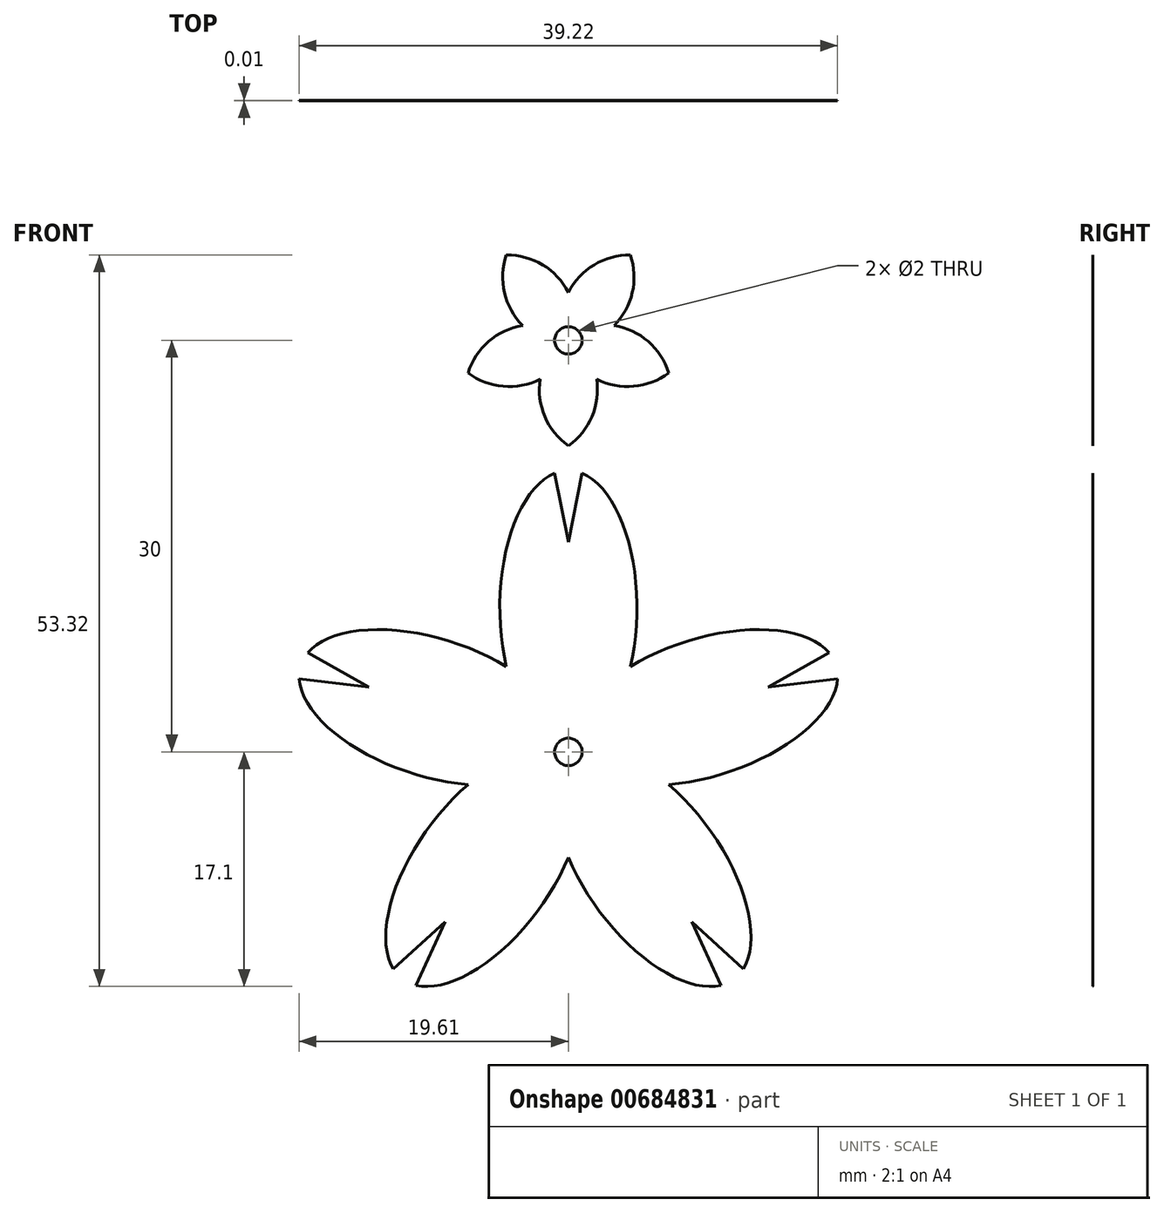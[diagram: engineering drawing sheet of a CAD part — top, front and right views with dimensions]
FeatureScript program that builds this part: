
annotation { "Feature Type Name" : "Feature", "Feature Type Description" : "" }
export const myFeature = defineFeature(function(context is Context, id is Id, definition is map)
    precondition{}
    {
        {
            var Q0;
            Q0=qCreatedBy(makeId("Front.planeOp"),FACE);
            var sketch = newSketch(context, id + "F0", { "sketchPlane" : qUnion([Q0])});
            skEllipticalArc(sketch, "E0", {});
            skLineSegment(sketch, "E1", {"start": v(0, 15.3) * mm, "end": v(1, 20.3) * mm});
            skLineSegment(sketch, "E2.MirrorCS", {"start": v(0, 15.3) * mm, "end": v(-1, 20.3) * mm});
            skEllipticalArc(sketch, "E3.1.0", {});
            skLineSegment(sketch, "E3.1.1", {"start": v(-14.55, 4.73) * mm, "end": v(-19.61, 5.32) * mm});
            skLineSegment(sketch, "E3.1.2", {"start": v(-14.55, 4.73) * mm, "end": v(-19, 7.22) * mm});
            skEllipticalArc(sketch, "E3.2.0", {});
            skLineSegment(sketch, "E3.2.1", {"start": v(-9, -12.38) * mm, "end": v(-11.12, -17) * mm});
            skLineSegment(sketch, "E3.2.2", {"start": v(-9, -12.38) * mm, "end": v(-12.74, -15.83) * mm});
            skEllipticalArc(sketch, "E3.3.0", {});
            skLineSegment(sketch, "E3.3.1", {"start": v(9, -12.38) * mm, "end": v(12.74, -15.83) * mm});
            skLineSegment(sketch, "E3.3.2", {"start": v(9, -12.38) * mm, "end": v(11.12, -17) * mm});
            skEllipticalArc(sketch, "E3.4.0", {});
            skLineSegment(sketch, "E3.4.1", {"start": v(14.55, 4.73) * mm, "end": v(19, 7.22) * mm});
            skLineSegment(sketch, "E3.4.2", {"start": v(14.55, 4.73) * mm, "end": v(19.61, 5.32) * mm});
            skPoint(sketch, "E3.center", {"position": v(0, 0) * mm});
            const initialGuessF0  = {"E0": [0, 0.0105, 0, 1, 0.01, 0.005, 0.20135792079033113, 6.081827386389255], "E3.1.0": [-0.009986093421099114, 0.0032446784409369493, -0.9510565162951536, 0.30901699437494723, 0.01, 0.005, 0.20135792079033066, 6.0818273863892545], "E3.2.0": [-0.006171745149070969, -0.008494678440936947, -0.587785252292473, -0.8090169943749476, 0.01, 0.005, 0.20135792079033082, 6.0818273863892545], "E3.3.0": [0.006171745149070967, -0.00849467844093695, 0.5877852522924732, -0.8090169943749473, 0.01, 0.005, 0.20135792079033088, 6.0818273863892545], "E3.4.0": [0.009986093421099114, 0.0032446784409369493, 0.9510565162951536, 0.3090169943749475, 0.01, 0.005, 0.20135792079033107, 6.081827386389255]};
            skSetInitialGuess(sketch, initialGuessF0);
            skSolve(sketch);
        }
        {
            var Q0;
            Q0=qCreatedBy(makeId("Front.planeOp"),FACE);
            var sketch = newSketch(context, id + "F1", { "sketchPlane" : qUnion([Q0])});
            skLineSegment(sketch, "E4.0", {"start": v(0, 15.3) * mm, "end": v(-1, 20.3) * mm});
            skLineSegment(sketch, "E5.0", {"start": v(0, 15.3) * mm, "end": v(1, 20.3) * mm});
            skEllipticalArc(sketch, "E6.0", {});
            skLineSegment(sketch, "E7.0", {"start": v(14.55, 4.73) * mm, "end": v(19, 7.22) * mm});
            skLineSegment(sketch, "E8.0", {"start": v(14.55, 4.73) * mm, "end": v(19.61, 5.32) * mm});
            skEllipticalArc(sketch, "E9.0", {});
            skLineSegment(sketch, "E10.0", {"start": v(9, -12.38) * mm, "end": v(11.12, -17) * mm});
            skLineSegment(sketch, "E11.0", {"start": v(9, -12.38) * mm, "end": v(12.74, -15.83) * mm});
            skEllipticalArc(sketch, "E12.0", {});
            skLineSegment(sketch, "E13.0", {"start": v(-9, -12.38) * mm, "end": v(-12.74, -15.83) * mm});
            skLineSegment(sketch, "E14.0", {"start": v(-9, -12.38) * mm, "end": v(-11.12, -17) * mm});
            skEllipticalArc(sketch, "E15.0", {});
            skLineSegment(sketch, "E16.0", {"start": v(-14.55, 4.73) * mm, "end": v(-19.61, 5.32) * mm});
            skLineSegment(sketch, "E17.0", {"start": v(-14.55, 4.73) * mm, "end": v(-19, 7.22) * mm});
            skEllipticalArc(sketch, "E18.trimOffspring", {});
            skEllipticalArc(sketch, "E19.trimOffspring", {});
            skEllipticalArc(sketch, "E20.trimOffspring", {});
            skEllipticalArc(sketch, "E21.trimOffspring", {});
            skCircle(sketch, "E22", {"center": v(0, 0) * mm, "radius": 1 * mm});
            skEllipticalArc(sketch, "E23.0", {});
            skEllipticalArc(sketch, "E24.MirrorCS", {});
            const initialGuessF1  = {"E6.0": [0.009986093421099114, 0.0032446784409369493, 0.9510565162951536, 0.3090169943749475, 0.01, 0.005, 0.20135792079033046, 2.0131203889968834], "E9.0": [0.006171745149070967, -0.00849467844093695, 0.5877852522924732, -0.8090169943749473, 0.01, 0.005, 0.20135792079033088, 2.0131203889969314], "E12.0": [-0.006171745149070969, -0.008494678440936947, -0.587785252292473, -0.8090169943749476, 0.01, 0.005, 0.20135792079033066, 2.013120388996931], "E15.0": [-0.009986093421099114, 0.0032446784409369493, -0.9510565162951536, 0.30901699437494723, 0.01, 0.005, 0.20135792079033066, 2.0131203889969314], "E18.trimOffspring": [-0.009986093421099114, 0.0032446784409369493, -0.9510565162951536, 0.30901699437494723, 0.01, 0.005, 4.270064918182703, 6.0818273863892545], "E19.trimOffspring": [-0.006171745149070969, -0.008494678440936947, -0.587785252292473, -0.8090169943749476, 0.01, 0.005, 4.270064918182655, 6.081827386389254], "E20.trimOffspring": [0.006171745149070967, -0.00849467844093695, 0.5877852522924732, -0.8090169943749473, 0.01, 0.005, 4.270064918182655, 6.0818273863892545], "E21.trimOffspring": [0.009986093421099114, 0.0032446784409369493, 0.9510565162951536, 0.3090169943749475, 0.01, 0.005, 4.270064918182655, 6.081827386389255], "E23.0": [0, 0.0105, 0, 1, 0.01, 0.005, 0.2013579207903312, 2.0131203889968976], "E24.MirrorCS": [0, 0.0105, 0, 1, 0.01, 0.005, 4.270064918182689, 6.081827386389255]};
            skSetInitialGuess(sketch, initialGuessF1);
            skSolve(sketch);
        }
        {
            var Q0;
            Q0=qCreatedBy(makeId("Front.planeOp"),FACE);
            var sketch = newSketch(context, id + "F2", { "sketchPlane" : qUnion([Q0])});
            skCircle(sketch, "E25.0", {"center": v(0, 0) * mm, "radius": 1 * mm});
            skArc(sketch, "E26", {"start": v(0, 3.5) * mm, "mid": v(-1.87, 5.5) * mm, "end": v(-4.52, 6.22) * mm});
            skArc(sketch, "E27.MirrorCS", {"start": v(0, 3.5) * mm, "mid": v(1.87, 5.5) * mm, "end": v(4.52, 6.22) * mm});
            skArc(sketch, "E28.1.0", {"start": v(-3.33, 1.08) * mm, "mid": v(-4.66, 3.48) * mm, "end": v(-4.52, 6.22) * mm});
            skArc(sketch, "E28.1.1", {"start": v(-3.33, 1.08) * mm, "mid": v(-5.81, -0.08) * mm, "end": v(-7.31, -2.38) * mm});
            skArc(sketch, "E28.2.0", {"start": v(-2.06, -2.83) * mm, "mid": v(-4.75, -3.35) * mm, "end": v(-7.31, -2.38) * mm});
            skArc(sketch, "E28.2.1", {"start": v(-2.06, -2.83) * mm, "mid": v(-1.72, -5.55) * mm, "end": v(0, -7.69) * mm});
            skArc(sketch, "E28.3.0", {"start": v(2.06, -2.83) * mm, "mid": v(1.72, -5.55) * mm, "end": v(0, -7.69) * mm});
            skArc(sketch, "E28.3.1", {"start": v(2.06, -2.83) * mm, "mid": v(4.75, -3.35) * mm, "end": v(7.31, -2.38) * mm});
            skArc(sketch, "E28.4.0", {"start": v(3.33, 1.08) * mm, "mid": v(5.81, -0.08) * mm, "end": v(7.31, -2.38) * mm});
            skArc(sketch, "E28.4.1", {"start": v(3.33, 1.08) * mm, "mid": v(4.66, 3.48) * mm, "end": v(4.52, 6.22) * mm});
            skSolve(sketch);
        }
        {
            var Q0;
            Q0=makeQuery(id+"F1.imprint","IMPRINT",FACE,{"disambiguationData":[TD([[makeQuery(id+"F1.imprint","IMPRINT",EDGE,{"derivedFrom":sQuery(id+"F1.wireOp",EDGE,"E4.0")}),1.0]])]});
            extrude(context, id + "F3", {"entities" : qUnion([Q0]), "depth" : 0.01 * mm, "offsetDistance" : 25 * mm});
        }
        {
            var Q0;
            Q0 = qSketchRegion(id + "F2", true);
            extrude(context, id + "F4", {"entities" : qUnion([Q0]), "depth" : 0.01 * mm, "offsetDistance" : 25 * mm});
        }
        {
            var Q0;
            Q0=makeQuery(id+"F4.opExtrude","SWEPT_BODY",BODY,{"disambiguationData":[OSD([sQuery(id+"F2.wireOp",EDGE,"E25.0"),sQuery(id+"F2.wireOp",EDGE,"E26"),sQuery(id+"F2.wireOp",EDGE,"E27.MirrorCS"),sQuery(id+"F2.wireOp",EDGE,"E28.1.0"),sQuery(id+"F2.wireOp",EDGE,"E28.1.1"),sQuery(id+"F2.wireOp",EDGE,"E28.2.0"),sQuery(id+"F2.wireOp",EDGE,"E28.2.1"),sQuery(id+"F2.wireOp",EDGE,"E28.3.0"),sQuery(id+"F2.wireOp",EDGE,"E28.3.1"),sQuery(id+"F2.wireOp",EDGE,"E28.4.0"),sQuery(id+"F2.wireOp",EDGE,"E28.4.1")])]});
            transform(context, id + "F5", {"entities" : qUnion([Q0]), "transformType" : TransformType.TRANSLATION_3D, "dx" : 0 * mm, "dy" : 0 * mm, "dz" : 30 * mm, "makeCopy" : false});
        }
    });
